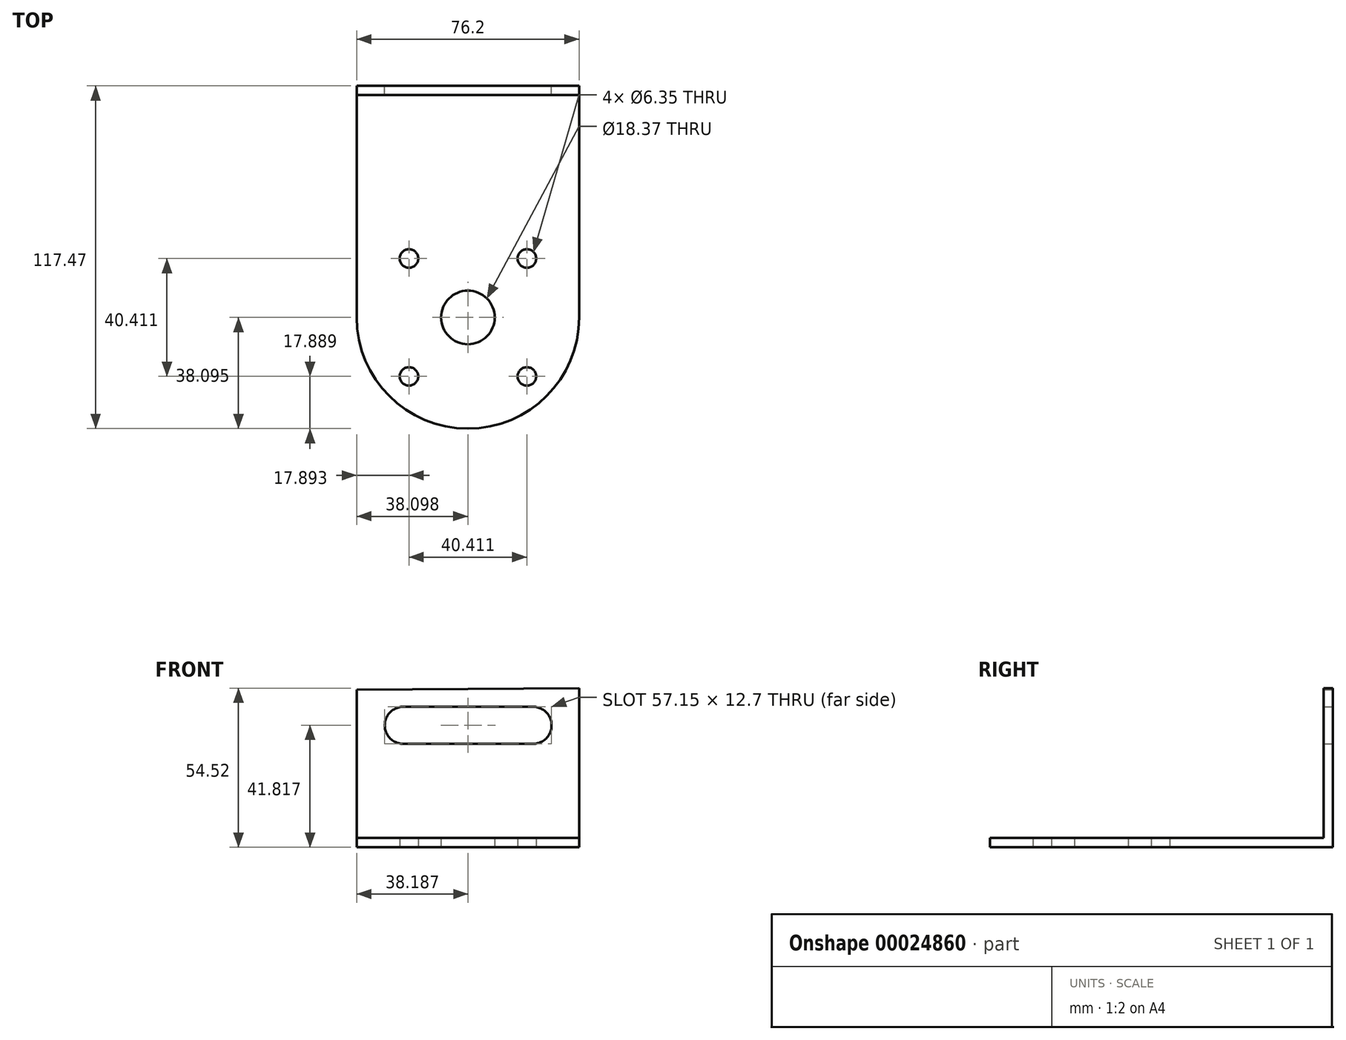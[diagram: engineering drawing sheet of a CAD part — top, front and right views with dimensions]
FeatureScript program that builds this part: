
annotation { "Feature Type Name" : "Feature", "Feature Type Description" : "" }
export const myFeature = defineFeature(function(context is Context, id is Id, definition is map)
    precondition{}
    {
        {
            var Q0;
            Q0=qCreatedBy(makeId("Front.planeOp"),FACE);
            var sketch = newSketch(context, id + "F0", { "sketchPlane" : qUnion([Q0])});
            skLineSegment(sketch, "E0", {"start": v(-77.25, 55.41) * mm, "end": v(-77.25, 1.44) * mm});
            skLineSegment(sketch, "E1", {"start": v(-77.25, 1.44) * mm, "end": v(-1.05, 1.44) * mm});
            skLineSegment(sketch, "E2", {"start": v(-1.05, 1.44) * mm, "end": v(-1.05, 55.96) * mm});
            skLineSegment(sketch, "E3", {"start": v(-1.05, 55.96) * mm, "end": v(-77.25, 55.41) * mm});
            skLineSegment(sketch, "E4", {"start": v(-77.25, 43.26) * mm, "end": v(-1.05, 43.26) * mm, "construction": true});
            skLineSegment(sketch, "E5", {"start": v(-61.38, 55.53) * mm, "end": v(-60.99, 1.44) * mm, "construction": true});
            skLineSegment(sketch, "E6", {"start": v(-16.93, 55.84) * mm, "end": v(-16.54, 1.44) * mm, "construction": true});
            skArc(sketch, "E7", {"start": v(-61.24, 49.6) * mm, "mid": v(-67.64, 43.26) * mm, "end": v(-61.24, 36.9) * mm});
            skArc(sketch, "E8", {"start": v(-16.88, 36.9) * mm, "mid": v(-10.49, 43.26) * mm, "end": v(-16.88, 49.6) * mm});
            skLineSegment(sketch, "E9", {"start": v(-61.24, 49.6) * mm, "end": v(-16.88, 49.6) * mm});
            skLineSegment(sketch, "E10", {"start": v(-61.24, 36.9) * mm, "end": v(-16.88, 36.9) * mm});
            skSolve(sketch);
        }
        {
            var Q0;
            Q0=makeQuery(id+"F0.imprint","IMPRINT",FACE,{"disambiguationData":[TD([[makeQuery(id+"F0.imprint","IMPRINT",EDGE,{"derivedFrom":sQuery(id+"F0.wireOp",EDGE,"E0")}),1.0]])]});
            extrude(context, id + "F1", {"entities" : qUnion([Q0]), "depth" : 3.17 * mm});
        }
        {
            var Q0;
            Q0=makeQuery(id+"F1.opExtrude","CAP_FACE",FACE,{"disambiguationData":[OSD([sQuery(id+"F0.wireOp",EDGE,"E0"),sQuery(id+"F0.wireOp",EDGE,"E1"),sQuery(id+"F0.wireOp",EDGE,"E2"),sQuery(id+"F0.wireOp",EDGE,"E3"),sQuery(id+"F0.wireOp",EDGE,"E7"),sQuery(id+"F0.wireOp",EDGE,"E8"),sQuery(id+"F0.wireOp",EDGE,"E9"),sQuery(id+"F0.wireOp",EDGE,"E10")])],"isStart":false});
            var sketch = newSketch(context, id + "F2", { "sketchPlane" : qUnion([Q0])});
            skLineSegment(sketch, "E11", {"start": v(-77.25, 4.61) * mm, "end": v(-1.05, 4.61) * mm});
            skSolve(sketch);
        }
        {
            var Q0;
            {var subQ1=sQuery(id+"F2.wireOp",EDGE,"E11");Q0=makeQuery(id+"F2.imprint","IMPRINT",FACE,{"disambiguationData":[TD([[makeQuery(id+"F2.imprint","IMPRINT",EDGE,{"derivedFrom":subQ1}),-1.0]])]});}
            extrude(context, id + "F3", {"entities" : qUnion([Q0]), "operationType" : NewBodyOperationType.ADD, "depth" : 76.2 * mm});
        }
        {
            var Q0;
            {var subQ0=sQuery(id+"F0.wireOp",EDGE,"E1");Q0=makeQuery(id+"F3.boolean.opBoolean","MERGE",FACE,{"derivedFrom":[makeQuery(id+"F1.opExtrude","SWEPT_FACE",FACE,{"disambiguationData":[OSD([subQ0])]}),makeQuery(id+"F3.opExtrude","SWEPT_FACE",FACE,{"disambiguationData":[OSD([subQ0])]})]});}
            var sketch = newSketch(context, id + "F4", { "sketchPlane" : qUnion([Q0])});
            skCircle(sketch, "E12", {"center": v(-39.15, 79.38) * mm, "radius": 38.1 * mm});
            skSolve(sketch);
        }
        {
            var Q0;
            {var subQ0=sQuery(id+"F0.wireOp",EDGE,"E1");var subQ1=makeQuery(id+"F3.opExtrude","CAP_EDGE",EDGE,{"disambiguationData":[OSD([subQ0])],"isStart":false});Q0=makeQuery(id+"F4.imprint","IMPRINT",FACE,{"disambiguationData":[TD([[makeQuery(id+"F4.imprint","IMPRINT",EDGE,{"derivedFrom":subQ1}),1.0]])]});}
            extrude(context, id + "F5", {"entities" : qUnion([Q0]), "operationType" : NewBodyOperationType.ADD, "oppositeDirection" : true, "depth" : 3.17 * mm});
        }
        {
            var Q0;
            {var subQ0=sQuery(id+"F0.wireOp",EDGE,"E1");Q0=makeQuery(id+"F5.boolean.opBoolean","MERGE",FACE,{"derivedFrom":[makeQuery(id+"F3.boolean.opBoolean","MERGE",FACE,{"derivedFrom":[makeQuery(id+"F1.opExtrude","SWEPT_FACE",FACE,{"disambiguationData":[OSD([subQ0])]}),makeQuery(id+"F3.opExtrude","SWEPT_FACE",FACE,{"disambiguationData":[OSD([subQ0])]})]}),makeQuery(id+"F5.opExtrude","CAP_FACE",FACE,{"disambiguationData":[OSD([subQ0,sQuery(id+"F4.wireOp",EDGE,"E12")])],"isStart":true})]});}
            var sketch = newSketch(context, id + "F6", { "sketchPlane" : qUnion([Q0])});
            skLineSegment(sketch, "E13", {"start": v(-77.25, 79.38) * mm, "end": v(-1.05, 79.38) * mm, "construction": true});
            skLineSegment(sketch, "E14", {"start": v(-39.15, 79.38) * mm, "end": v(-39.15, 117.47) * mm, "construction": true});
            skCircle(sketch, "E15", {"center": v(-39.15, 79.38) * mm, "radius": 9.19 * mm});
            skCircle(sketch, "E16", {"center": v(-39.15, 79.38) * mm, "radius": 28.58 * mm, "construction": true});
            skLineSegment(sketch, "E17", {"start": v(-39.15, 79.38) * mm, "end": v(-84.07, 79.38) * mm, "construction": true});
            skLineSegment(sketch, "E18", {"start": v(-39.15, 79.38) * mm, "end": v(-71.72, 111.95) * mm, "construction": true});
            skCircle(sketch, "E19", {"center": v(-59.36, 99.58) * mm, "radius": 3.18 * mm});
            skCircle(sketch, "E20.1.0", {"center": v(-59.36, 59.17) * mm, "radius": 3.18 * mm});
            skCircle(sketch, "E20.2.0", {"center": v(-18.95, 59.17) * mm, "radius": 3.18 * mm});
            skCircle(sketch, "E21.1.3.0", {"center": v(-18.95, 99.58) * mm, "radius": 3.18 * mm});
            skSolve(sketch);
        }
        {
            var Q0;
            Q0=makeQuery(id+"F6.imprint","IMPRINT",FACE,{"disambiguationData":[TD([[makeQuery(id+"F6.imprint","IMPRINT",EDGE,{"derivedFrom":sQuery(id+"F6.wireOp",EDGE,"E19")}),1.0]])]});
            var Q1;
            Q1=makeQuery(id+"F6.imprint","IMPRINT",FACE,{"disambiguationData":[TD([[makeQuery(id+"F6.imprint","IMPRINT",EDGE,{"derivedFrom":sQuery(id+"F6.wireOp",EDGE,"E21.1.3.0")}),1.0]])]});
            var Q2;
            Q2=makeQuery(id+"F6.imprint","IMPRINT",FACE,{"disambiguationData":[TD([[makeQuery(id+"F6.imprint","IMPRINT",EDGE,{"derivedFrom":sQuery(id+"F6.wireOp",EDGE,"E15")}),1.0]])]});
            var Q3;
            Q3=makeQuery(id+"F6.imprint","IMPRINT",FACE,{"disambiguationData":[TD([[makeQuery(id+"F6.imprint","IMPRINT",EDGE,{"derivedFrom":sQuery(id+"F6.wireOp",EDGE,"E20.2.0")}),1.0]])]});
            var Q4;
            Q4=makeQuery(id+"F6.imprint","IMPRINT",FACE,{"disambiguationData":[TD([[makeQuery(id+"F6.imprint","IMPRINT",EDGE,{"derivedFrom":sQuery(id+"F6.wireOp",EDGE,"E20.1.0")}),1.0]])]});
            extrude(context, id + "F7", {"entities" : qUnion([Q0, Q1, Q2, Q3, Q4]), "operationType" : NewBodyOperationType.REMOVE, "oppositeDirection" : true, "depth" : 46.67 * mm});
        }
    });
